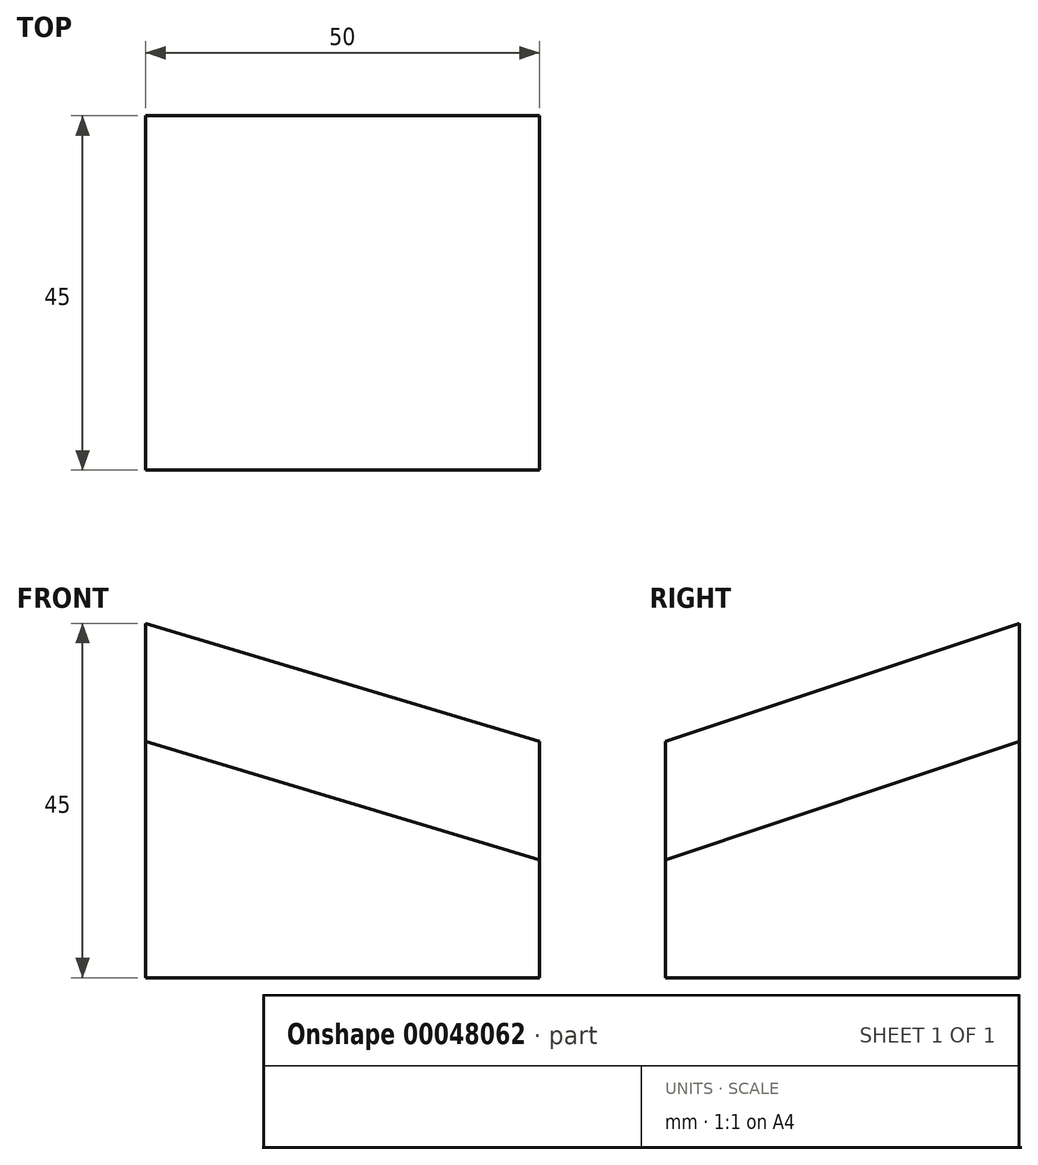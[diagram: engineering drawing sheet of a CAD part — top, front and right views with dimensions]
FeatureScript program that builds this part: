
annotation { "Feature Type Name" : "Feature", "Feature Type Description" : "" }
export const myFeature = defineFeature(function(context is Context, id is Id, definition is map)
    precondition{}
    {
        {
            var Q0;
            Q0=qCreatedBy(makeId("Right.planeOp"),FACE);
            var sketch = newSketch(context, id + "F0", { "sketchPlane" : qUnion([Q0])});
            skLineSegment(sketch, "E0", {"start": v(0, 0) * mm, "end": v(0, 45) * mm});
            skLineSegment(sketch, "E1", {"start": v(0, 45) * mm, "end": v(-45, 30) * mm});
            skLineSegment(sketch, "E2", {"start": v(-45, 30) * mm, "end": v(-45, 0) * mm});
            skLineSegment(sketch, "E3", {"start": v(-45, 0) * mm, "end": v(0, 0) * mm});
            skSolve(sketch);
        }
        {
            var Q0;
            Q0=makeQuery(id+"F0.imprint","IMPRINT",FACE,{"disambiguationData":[TD([[makeQuery(id+"F0.imprint","IMPRINT",EDGE,{"derivedFrom":sQuery(id+"F0.wireOp",EDGE,"E0")}),1.0]])]});
            cPlane(context, id + "F1", {"entities" : qUnion([Q0]), "cplaneType" : CPlaneType.OFFSET, "offset" : 50 * mm, "width" : 150 * mm, "height" : 150 * mm});
        }
        {
            var Q0;
            Q0=qCreatedBy(id+"F1.planeOp",FACE);
            var sketch = newSketch(context, id + "F2", { "sketchPlane" : qUnion([Q0])});
            skLineSegment(sketch, "E4", {"start": v(0, 0) * mm, "end": v(0, 30) * mm});
            skLineSegment(sketch, "E5", {"start": v(0, 30) * mm, "end": v(-45, 15) * mm});
            skLineSegment(sketch, "E6", {"start": v(-45, 15) * mm, "end": v(-45, 0) * mm});
            skLineSegment(sketch, "E7", {"start": v(-45, 0) * mm, "end": v(0, 0) * mm});
            skSolve(sketch);
        }
        {
            var Q0;
            Q0=makeQuery(id+"F0.imprint","IMPRINT",FACE,{"disambiguationData":[TD([[makeQuery(id+"F0.imprint","IMPRINT",EDGE,{"derivedFrom":sQuery(id+"F0.wireOp",EDGE,"E0")}),1.0]])]});
            var Q1;
            Q1=makeQuery(id+"F2.imprint","IMPRINT",FACE,{"disambiguationData":[TD([[makeQuery(id+"F2.imprint","IMPRINT",EDGE,{"derivedFrom":sQuery(id+"F2.wireOp",EDGE,"E4")}),1.0]])]});
            loft(context, id + "F3", {"sheetProfilesArray" : [{ "sheetProfileEntities" : qUnion([Q0]) }, { "sheetProfileEntities" : qUnion([Q1]) }]});
        }
    });
